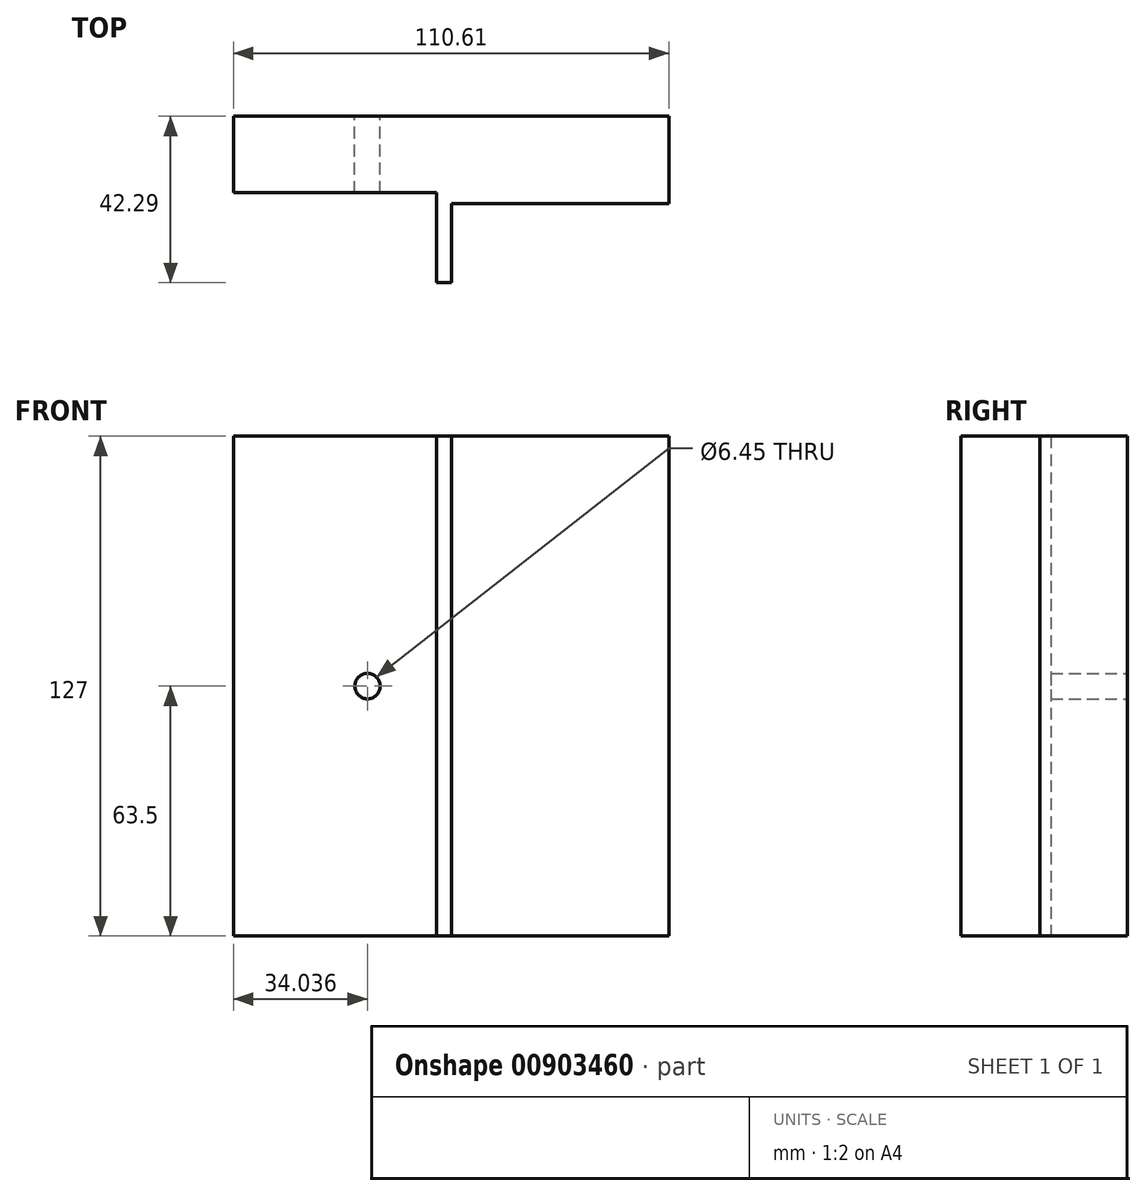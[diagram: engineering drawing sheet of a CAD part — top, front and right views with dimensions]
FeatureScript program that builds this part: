
annotation { "Feature Type Name" : "Feature", "Feature Type Description" : "" }
export const myFeature = defineFeature(function(context is Context, id is Id, definition is map)
    precondition{}
    {
        {
            var Q0;
            Q0=qCreatedBy(makeId("Top.planeOp"),FACE);
            var sketch = newSketch(context, id + "F0", { "sketchPlane" : qUnion([Q0])});
            skLineSegment(sketch, "E0.bottom", {"start": v(0, 0) * mm, "end": v(110.6, 0) * mm});
            skLineSegment(sketch, "E0.top", {"start": v(0, 19.43) * mm, "end": v(110.6, 19.43) * mm});
            skLineSegment(sketch, "E0.left", {"start": v(0, 0) * mm, "end": v(0, 19.43) * mm});
            skLineSegment(sketch, "E0.right", {"start": v(110.6, 0) * mm, "end": v(110.6, 19.43) * mm});
            skLineSegment(sketch, "E1", {"start": v(51.64, 0) * mm, "end": v(51.64, -22.86) * mm});
            skLineSegment(sketch, "E2", {"start": v(51.64, -22.86) * mm, "end": v(55.45, -22.86) * mm});
            skLineSegment(sketch, "E3", {"start": v(55.45, -22.86) * mm, "end": v(55.45, -2.8) * mm});
            skLineSegment(sketch, "E4", {"start": v(55.45, -2.8) * mm, "end": v(110.6, -2.8) * mm});
            skLineSegment(sketch, "E5", {"start": v(110.6, -2.8) * mm, "end": v(110.6, 0) * mm});
            skLineSegment(sketch, "E6", {"start": v(110.6, 0) * mm, "end": v(110.6, 0) * mm});
            skSolve(sketch);
        }
        {
            var Q0;
            Q0 = qSketchRegion(id + "F0", true);
            extrude(context, id + "F1", {"entities" : qUnion([Q0]), "depth" : 127 * mm, "offsetDistance" : 25.4 * mm});
        }
        {
            var Q0;
            Q0=makeQuery(id+"F1.opExtrude","SWEPT_FACE",FACE,{"disambiguationData":[OSD([sQuery(id+"F0.wireOp",EDGE,"E0.top")])]});
            var sketch = newSketch(context, id + "F2", { "sketchPlane" : qUnion([Q0])});
            skCircle(sketch, "E7", {"center": v(-34.04, 63.5) * mm, "radius": 3.23 * mm});
            skLineSegment(sketch, "E8", {"start": v(-34.04, 63.5) * mm, "end": v(0, 63.5) * mm, "construction": true});
            skSolve(sketch);
        }
        {
            var Q0;
            Q0 = qSketchRegion(id + "F2", true);
            extrude(context, id + "F3", {"entities" : qUnion([Q0]), "operationType" : NewBodyOperationType.REMOVE, "endBound" : BoundingType.UP_TO_NEXT, "oppositeDirection" : true, "depth" : 25.4 * mm, "offsetDistance" : 25.4 * mm});
        }
    });
